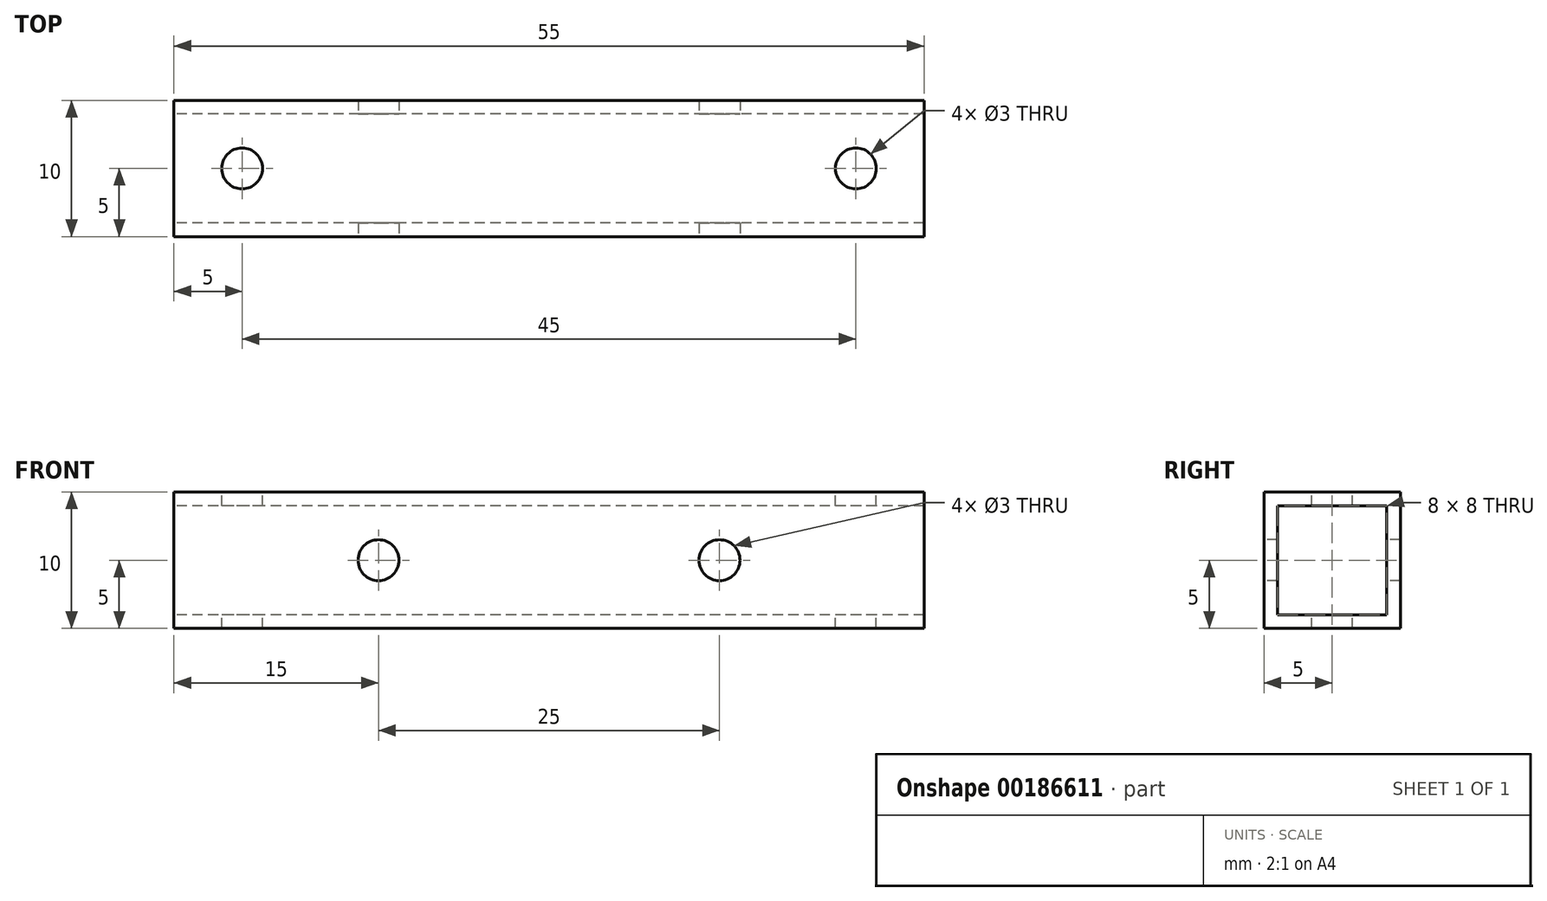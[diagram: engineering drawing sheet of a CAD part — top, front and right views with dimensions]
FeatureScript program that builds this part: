
annotation { "Feature Type Name" : "Feature", "Feature Type Description" : "" }
export const myFeature = defineFeature(function(context is Context, id is Id, definition is map)
    precondition{}
    {
        {
            var Q0;
            Q0=qCreatedBy(makeId("Right.planeOp"),FACE);
            var sketch = newSketch(context, id + "F0", { "sketchPlane" : qUnion([Q0])});
            skLineSegment(sketch, "E0.bottom", {"start": v(-5, -5) * mm, "end": v(5, -5) * mm});
            skLineSegment(sketch, "E0.top", {"start": v(-5, 5) * mm, "end": v(5, 5) * mm});
            skLineSegment(sketch, "E0.left", {"start": v(-5, -5) * mm, "end": v(-5, 5) * mm});
            skLineSegment(sketch, "E0.right", {"start": v(5, -5) * mm, "end": v(5, 5) * mm});
            skPoint(sketch, "E0.middle", {"position": v(0, 0) * mm});
            skLineSegment(sketch, "E1.bottom", {"start": v(-4, -4) * mm, "end": v(4, -4) * mm});
            skLineSegment(sketch, "E1.top", {"start": v(-4, 4) * mm, "end": v(4, 4) * mm});
            skLineSegment(sketch, "E1.left", {"start": v(-4, -4) * mm, "end": v(-4, 4) * mm});
            skLineSegment(sketch, "E1.right", {"start": v(4, -4) * mm, "end": v(4, 4) * mm});
            skSolve(sketch);
        }
        {
            var Q0;
            Q0 = qSketchRegion(id + "F0", true);
            extrude(context, id + "F1", {"entities" : qUnion([Q0]), "depth" : 55 * mm});
        }
        {
            var Q0;
            Q0=makeQuery(id+"F1.opExtrude","SWEPT_FACE",FACE,{"disambiguationData":[OSD([sQuery(id+"F0.wireOp",EDGE,"E0.top")])]});
            var sketch = newSketch(context, id + "F2", { "sketchPlane" : qUnion([Q0])});
            skLineSegment(sketch, "E2", {"start": v(55, 0) * mm, "end": v(0, 0) * mm, "construction": true});
            skCircle(sketch, "E3", {"center": v(5, 0) * mm, "radius": 1.5 * mm});
            skLineSegment(sketch, "E4", {"start": v(27.5, 5) * mm, "end": v(27.5, -5) * mm, "construction": true});
            skCircle(sketch, "E5.MirrorC", {"center": v(50, 0) * mm, "radius": 1.5 * mm});
            skSolve(sketch);
        }
        {
            var Q0;
            Q0 = qSketchRegion(id + "F2", true);
            extrude(context, id + "F3", {"entities" : qUnion([Q0]), "operationType" : NewBodyOperationType.REMOVE, "oppositeDirection" : true, "depth" : 25 * mm});
        }
        {
            var Q0;
            Q0=makeQuery(id+"F1.opExtrude","SWEPT_FACE",FACE,{"disambiguationData":[OSD([sQuery(id+"F0.wireOp",EDGE,"E0.left")])]});
            var sketch = newSketch(context, id + "F4", { "sketchPlane" : qUnion([Q0])});
            skLineSegment(sketch, "E6", {"start": v(0, 0) * mm, "end": v(55, 0) * mm, "construction": true});
            skLineSegment(sketch, "E7", {"start": v(27.5, 5) * mm, "end": v(27.5, -5) * mm, "construction": true});
            skCircle(sketch, "E8", {"center": v(15, 0) * mm, "radius": 1.5 * mm});
            skCircle(sketch, "E9.MirrorC", {"center": v(40, 0) * mm, "radius": 1.5 * mm});
            skSolve(sketch);
        }
        {
            var Q0;
            Q0 = qSketchRegion(id + "F4", true);
            extrude(context, id + "F5", {"entities" : qUnion([Q0]), "operationType" : NewBodyOperationType.REMOVE, "oppositeDirection" : true, "depth" : 25 * mm});
        }
    });
